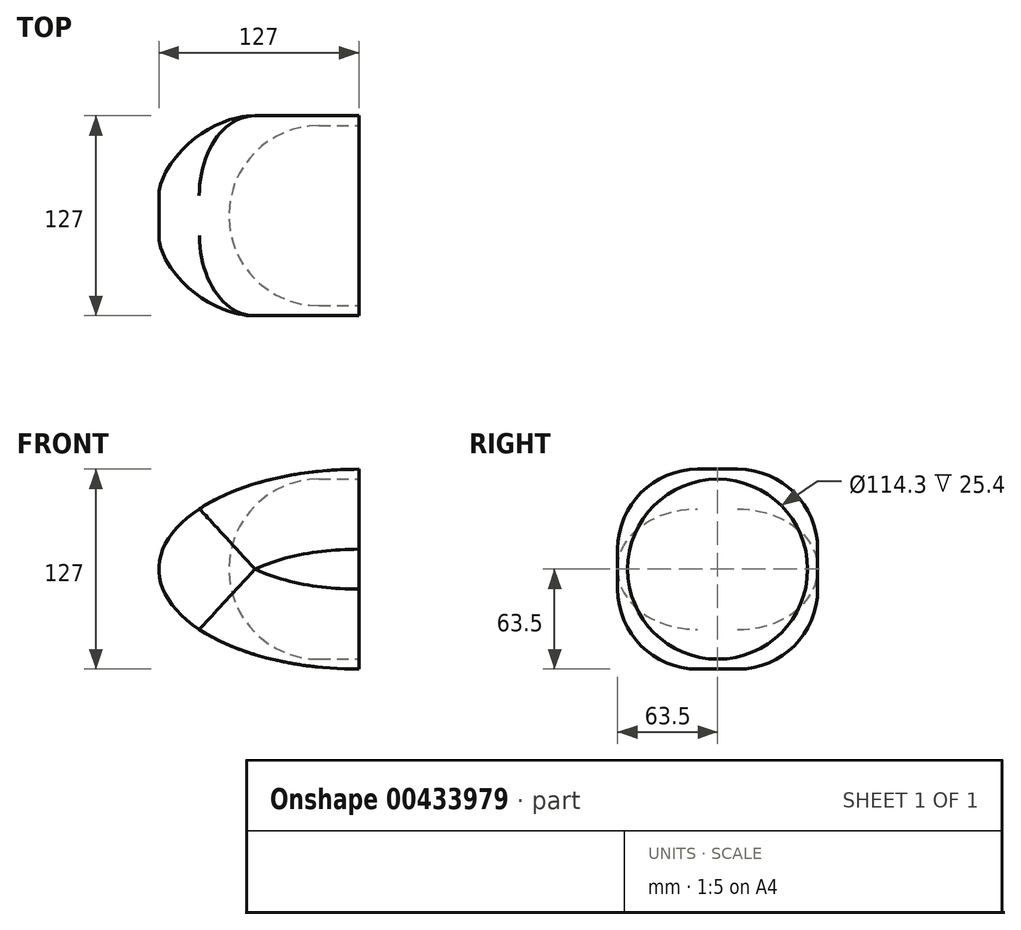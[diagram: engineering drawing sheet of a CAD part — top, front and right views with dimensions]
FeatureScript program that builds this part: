
annotation { "Feature Type Name" : "Feature", "Feature Type Description" : "" }
export const myFeature = defineFeature(function(context is Context, id is Id, definition is map)
    precondition{}
    {
        {
            var Q0;
            Q0=qCreatedBy(makeId("Front.planeOp"),FACE);
            var sketch = newSketch(context, id + "F0", { "sketchPlane" : qUnion([Q0])});
            skEllipticalArc(sketch, "E0", {});
            skLineSegment(sketch, "E1", {"start": v(0, 63.5) * mm, "end": v(0, -63.5) * mm});
            const initialGuessF0  = {"E0": [0, 0, -1, 0, 0.127, 0.0635, 4.71238898038469, 1.5707963267948966]};
            skSetInitialGuess(sketch, initialGuessF0);
            skSolve(sketch);
        }
        {
            var Q0;
            Q0=makeQuery(id+"F0.imprint","IMPRINT",FACE,{"disambiguationData":[TD([[makeQuery(id+"F0.imprint","IMPRINT",EDGE,{"derivedFrom":sQuery(id+"F0.wireOp",EDGE,"E0")}),1.0]])]});
            extrude(context, id + "F1", {"entities" : qUnion([Q0]), "depth" : 127 * mm});
        }
        {
            var Q0;
            Q0=makeQuery(id+"F1.opExtrude","CAP_EDGE",EDGE,{"disambiguationData":[OSD([sQuery(id+"F0.wireOp",EDGE,"E0")])],"isStart":false});
            var Q1;
            Q1=makeQuery(id+"F1.opExtrude","CAP_EDGE",EDGE,{"disambiguationData":[OSD([sQuery(id+"F0.wireOp",EDGE,"E0")])],"isStart":true});
            fillet(context, id + "F2", {"entities" : qUnion([Q0, Q1]), "radius" : 50.8 * mm, "tangentPropagation" : true, "allowEdgeOverflow" : false});
        }
        {
            var Q0;
            Q0=makeQuery(id+"F1.opExtrude","SWEPT_FACE",FACE,{"disambiguationData":[OSD([sQuery(id+"F0.wireOp",EDGE,"E1")])]});
            var sketch = newSketch(context, id + "F3", { "sketchPlane" : qUnion([Q0])});
            skLineSegment(sketch, "E2.0", {"start": v(-76.2, 63.5) * mm, "end": v(-50.8, 63.5) * mm});
            skLineSegment(sketch, "E3.0", {"start": v(-76.2, -63.5) * mm, "end": v(-50.8, -63.5) * mm});
            skLineSegment(sketch, "E4.0", {"start": v(0, 12.7) * mm, "end": v(0, -12.7) * mm});
            skLineSegment(sketch, "E5.0", {"start": v(-127, 12.7) * mm, "end": v(-127, -12.7) * mm});
            skLineSegment(sketch, "E6", {"start": v(-127, 0) * mm, "end": v(0, 0) * mm, "construction": true});
            skLineSegment(sketch, "E7", {"start": v(-63.5, 63.5) * mm, "end": v(-63.5, -63.5) * mm, "construction": true});
            skCircle(sketch, "E8", {"center": v(-63.5, 0) * mm, "radius": 57.15 * mm});
            skSolve(sketch);
        }
        {
            var Q0;
            Q0=makeQuery(id+"F3.imprint","IMPRINT",FACE,{"disambiguationData":[TD([[makeQuery(id+"F3.imprint","IMPRINT",EDGE,{"derivedFrom":sQuery(id+"F3.wireOp",EDGE,"E8")}),1.0]])]});
            extrude(context, id + "F4", {"entities" : qUnion([Q0]), "operationType" : NewBodyOperationType.REMOVE, "oppositeDirection" : true, "depth" : 25.4 * mm});
        }
        {
            var Q0;
            Q0=makeQuery(id+"F4.boolean.opBoolean","COPY",FACE,{"derivedFrom":makeQuery(id+"F4.opExtrude","CAP_FACE",FACE,{"disambiguationData":[OSD([sQuery(id+"F3.wireOp",EDGE,"E8")])],"isStart":false})});
            var sketch = newSketch(context, id + "F5", { "sketchPlane" : qUnion([Q0])});
            skCircle(sketch, "E9.0", {"center": v(-63.5, 0) * mm, "radius": 57.15 * mm});
            skLineSegment(sketch, "E10", {"start": v(-63.5, 57.15) * mm, "end": v(-63.5, -57.15) * mm});
            skSolve(sketch);
        }
        {
            var Q0;
            {var subQ0=sQuery(id+"F5.wireOp",EDGE,"E10");Q0=makeQuery(id+"F5.imprint","IMPRINT",FACE,{"disambiguationData":[TD([[makeQuery(id+"F5.imprint","IMPRINT",EDGE,{"derivedFrom":subQ0}),1.0]])]});}
            var Q1;
            Q1=sQuery(id+"F5.wireOp",EDGE,"E10");
            revolve(context, id + "F6", {"operationType" : NewBodyOperationType.REMOVE, "entities" : qUnion([Q0]), "axis" : qUnion([Q1]), "revolveType" : RevolveType.FULL, "oppositeDirection" : true});
        }
    });
